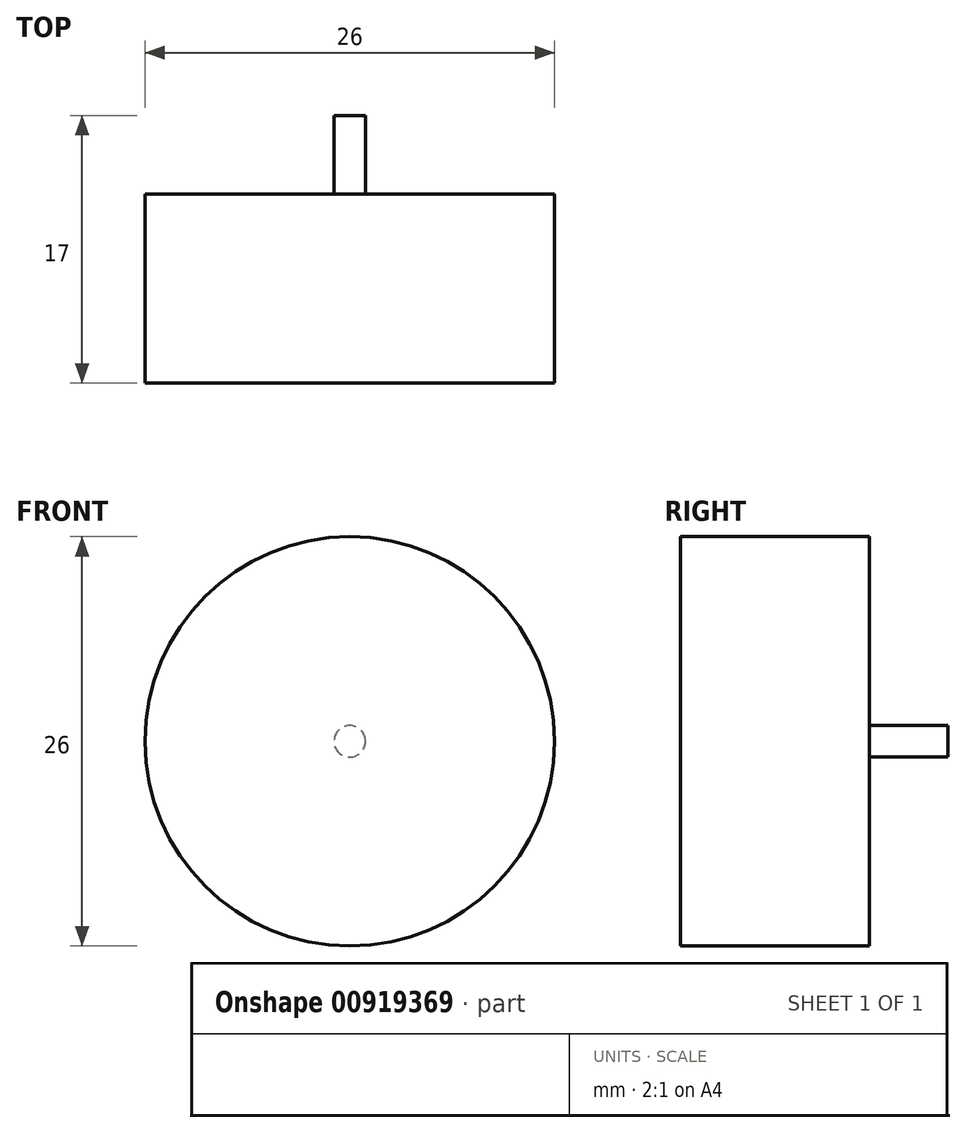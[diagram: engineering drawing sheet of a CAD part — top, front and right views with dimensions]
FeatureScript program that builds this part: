
annotation { "Feature Type Name" : "Feature", "Feature Type Description" : "" }
export const myFeature = defineFeature(function(context is Context, id is Id, definition is map)
    precondition{}
    {
        {
            var Q0;
            Q0=qCreatedBy(makeId("Front.planeOp"),FACE);
            var sketch = newSketch(context, id + "F0", { "sketchPlane" : qUnion([Q0])});
            skCircle(sketch, "E0", {"center": v(0, 0) * mm, "radius": 11.5 * mm});
            skCircle(sketch, "E1", {"center": v(0, 0) * mm, "radius": 13 * mm});
            skSolve(sketch);
        }
        {
            var Q0;
            Q0=makeQuery(id+"F0.imprint","IMPRINT",FACE,{"disambiguationData":[TD([[makeQuery(id+"F0.imprint","IMPRINT",EDGE,{"derivedFrom":sQuery(id+"F0.wireOp",EDGE,"E0")}),-1.0]])]});
            extrude(context, id + "F1", {"entities" : qUnion([Q0]), "endBound" : BoundingType.SYMMETRIC, "depth" : 12 * mm, "offsetDistance" : 25 * mm});
        }
        {
            var Q0;
            Q0=makeQuery(id+"F0.imprint","IMPRINT",FACE,{"disambiguationData":[TD([[makeQuery(id+"F0.imprint","IMPRINT",EDGE,{"derivedFrom":sQuery(id+"F0.wireOp",EDGE,"E0")}),1.0]])]});
            extrude(context, id + "F2", {"entities" : qUnion([Q0]), "operationType" : NewBodyOperationType.ADD, "endBound" : BoundingType.SYMMETRIC, "depth" : 12 * mm, "offsetDistance" : 25 * mm});
        }
        {
            var Q0;
            Q0=makeQuery(id+"F2.opExtrude","CAP_FACE",FACE,{"disambiguationData":[OSD([sQuery(id+"F0.wireOp",EDGE,"E0")])],"isStart":true});
            var sketch = newSketch(context, id + "F3", { "sketchPlane" : qUnion([Q0])});
            skCircle(sketch, "E2", {"center": v(0, 0) * mm, "radius": 1 * mm});
            skSolve(sketch);
        }
        {
            var Q0;
            Q0=makeQuery(id+"F3.imprint","IMPRINT",FACE,{"disambiguationData":[TD([[makeQuery(id+"F3.imprint","IMPRINT",EDGE,{"derivedFrom":sQuery(id+"F3.wireOp",EDGE,"E2")}),1.0]])]});
            extrude(context, id + "F4", {"entities" : qUnion([Q0]), "operationType" : NewBodyOperationType.ADD, "depth" : 5 * mm, "offsetDistance" : 25 * mm});
        }
    });
